# Revit family: Control_Unit-Lutron-DALI-Power_Module-QSN-2DALUNV-D
name_source: partatom
category: Lighting Devices
revit_build: Autodesk Revit 2018 (Build: 20170223_1515(x64)
units: mm (PartAtom-declared; Revit-internal decimal feet)

## family parameters
Cut with Voids When Loaded = No
Host = Face
Maintain Annotation Orientation = Yes
OmniClass Number = 23.80.30.11.17
OmniClass Title = Distribution Boards and Control Panels
Part Type = Normal
Room Calculation Point = No
Round Connector Dimension = Use Radius
Shared = No

## types (1)
- QSN-2DALUNV-D
    Assembly Code = D3060800
    Cost = 0 $
    Current = 0 A
    Default Elevation = 4' - 0"
    Description = DALI® Single master application controller
    Finish = Plastic - Lutron - White - Matte
    Frequency = 50|60 Hz
    Instruction Sheet Link = http://www.lutron.com
    Manufacturer = Lutron Electronics Co., Inc
    Manufacturer Fax Number = 610-282-1243
    Maximum Operating Temperature = 32 °F
    Minimum Operating Temperature = 104 °F
    Model = QSN-2DALUNV-D
    Number of Poles = 1
    Operating Voltage = 120/220-240 V~
    Overall Depth = 0' - 3 1/2"
    Overall Height = 0' - 2 3/8"
    Overall Width = 0' - 6 3/8"
    Performance URL = http://www.lutron.com
    Product Documentation Link = https://www.lutron.com
    Product Name = DALI® Power Module
    Product Page URL = https://www.lutron.com
    Series = Athena
    URL = http://www.lutron.com
    Version = 2018 - v1.0a
    Video Link = https://www.youtube.com
    Voltage = 120 V
    Warranty URL = http://www.lutron.com

## geometry (parser evidence)
native form markers: Sweep x3
no freeform markers — native parametric forms only
